# Revit family: Gravity_Intake_Roof_Ventilators-GLAB_Carnes
name_source: partatom
category: Mechanical Equipment
revit_build: Autodesk Revit Architecture 2012 (Build: 20110309_2315(x64)
units: mm (PartAtom-declared; Revit-internal decimal feet)

## types (117) — shared parameters
04 CSI = 23 34 23
95 CSI = 15830
Assembly Code = D3040200
Catalog URL = http://www.carnes.com
Default Elevation = 0' - 0"
Description = Gravity Intake Roof Ventilator
Housing = Aluminum-Carnes-Spun-Brushed
Manufacturer = Carnes Company
Manufacturer Fax = 608-845-6470
Material = Aluminum
Model = GLAB
Product Page URL = http://www.carnes.com
Specifications URL = http://www.carnes.com
Subcategory = Ventilation
URL = http://www.carnes.com
Warranty URL = http://www.carnes.com

## per-type parameters (varying)
| type | Curb Cap Length | Curb Cap Width | G | Hood Length | Hood Width | Intake Throat Velocity 1000 | Intake Throat Velocity 1200 | Intake Throat Velocity 400 | Intake Throat Velocity 500 | Intake Throat Velocity 600 | Intake Throat Velocity 700 | Intake Throat Velocity 800 | Intake Throat Velocity 900 | Louvers | Throat Area | Throat Size Length | Throat Size Width |
| 12x12 | 1' - 8" | 1' - 8" | 0' - 9 1/2" | 2' - 4" | 2' - 4" | 1000 | 1200 | 400 | 500 | 600 | 700 | 800 | 900 | 2 | 1.00 | 1' - 0" | 1' - 0" |
| 12x14 | 1' - 10" | 1' - 8" | 0' - 9 1/2" | 2' - 6" | 2' - 4" | 1167 | 1400 | 467 | 583 | 700 | 817 | 933 | 1050 | 2 | 1.17 | 1' - 2" | 1' - 0" |
| 12x16 | 2' - 0" | 1' - 8" | 0' - 9 1/2" | 2' - 8" | 2' - 4" | 1333 | 1600 | 533 | 667 | 800 | 933 | 1067 | 1200 | 2 | 1.33 | 1' - 4" | 1' - 0" |
| 12x18 | 2' - 2" | 1' - 8" | 0' - 9 1/2" | 2' - 10" | 2' - 4" | 1500 | 1800 | 600 | 750 | 900 | 1050 | 1200 | 1350 | 2 | 1.50 | 1' - 6" | 1' - 0" |
| 12x20 | 2' - 4" | 1' - 8" | 0' - 9 1/2" | 3' - 0" | 2' - 4" | 1667 | 2000 | 667 | 833 | 1000 | 1167 | 1333 | 1500 | 2 | 1.67 | 1' - 8" | 1' - 0" |
| 12x22 | 2' - 6" | 1' - 8" | 0' - 9 1/2" | 3' - 2" | 2' - 4" | 1833 | 2200 | 733 | 917 | 1100 | 1283 | 1467 | 1650 | 2 | 1.83 | 1' - 10" | 1' - 0" |
| 12x24 | 2' - 8" | 1' - 8" | 0' - 9 1/2" | 3' - 4" | 2' - 4" | 2000 | 2400 | 800 | 1000 | 1200 | 1400 | 1600 | 1800 | 2 | 2.00 | 2' - 0" | 1' - 0" |
| 12x30 | 3' - 2" | 1' - 8" | 0' - 9 1/2" | 3' - 10" | 2' - 4" | 2500 | 3000 | 1000 | 1250 | 1500 | 1750 | 2000 | 2250 | 2 | 2.50 | 2' - 6" | 1' - 0" |
| 12x36 | 3' - 8" | 1' - 8" | 0' - 9 1/2" | 4' - 4" | 2' - 4" | 3000 | 3600 | 1200 | 1500 | 1800 | 2100 | 2400 | 2700 | 2 | 3.00 | 3' - 0" | 1' - 0" |
| 12x42 | 4' - 2" | 1' - 8" | 0' - 9 1/2" | 4' - 10" | 2' - 4" | 3500 | 4200 | 1400 | 1750 | 2100 | 2450 | 2800 | 3150 | 2 | 3.50 | 3' - 6" | 1' - 0" |
| 12x48 | 4' - 8" | 1' - 8" | 0' - 9 1/2" | 5' - 4" | 2' - 4" | 4000 | 4800 | 1600 | 2000 | 2400 | 2800 | 3200 | 3600 | 2 | 4.00 | 4' - 0" | 1' - 0" |
| 12x54 | 5' - 2" | 1' - 8" | 0' - 9 1/2" | 5' - 10" | 2' - 4" | 4500 | 5400 | 1800 | 2250 | 2700 | 3150 | 3600 | 4050 | 2 | 4.50 | 4' - 6" | 1' - 0" |
| 14x14 | 1' - 10" | 1' - 10" | 0' - 9 1/2" | 2' - 6" | 2' - 6" | 1361 | 1633 | 544 | 681 | 817 | 953 | 1089 | 1225 | 2 | 1.36 | 1' - 2" | 1' - 2" |
| 14x16 | 2' - 0" | 1' - 10" | 0' - 9 1/2" | 2' - 8" | 2' - 6" | 1556 | 1867 | 622 | 778 | 933 | 1089 | 1244 | 1400 | 2 | 1.56 | 1' - 4" | 1' - 2" |
| 14x18 | 2' - 2" | 1' - 10" | 0' - 9 1/2" | 2' - 10" | 2' - 6" | 1750 | 2100 | 700 | 875 | 1050 | 1225 | 1400 | 1575 | 2 | 1.75 | 1' - 6" | 1' - 2" |
| 14x20 | 2' - 4" | 1' - 10" | 0' - 9 1/2" | 3' - 0" | 2' - 6" | 1944 | 2333 | 778 | 972 | 1167 | 1361 | 1556 | 1750 | 2 | 1.94 | 1' - 8" | 1' - 2" |
| 14x22 | 2' - 6" | 1' - 10" | 0' - 9 1/2" | 3' - 2" | 2' - 6" | 2139 | 2567 | 856 | 1069 | 1283 | 1497 | 1711 | 1925 | 2 | 2.14 | 1' - 10" | 1' - 2" |
| 14x24 | 2' - 8" | 1' - 10" | 0' - 9 1/2" | 3' - 4" | 2' - 6" | 2333 | 2800 | 933 | 1167 | 1400 | 1633 | 1867 | 2100 | 2 | 2.33 | 2' - 0" | 1' - 2" |
| 14x30 | 3' - 2" | 1' - 10" | 0' - 9 1/2" | 3' - 10" | 2' - 6" | 2917 | 3500 | 1167 | 1458 | 1750 | 2042 | 2333 | 2625 | 2 | 2.92 | 2' - 6" | 1' - 2" |
| 14x36 | 3' - 8" | 1' - 10" | 0' - 9 1/2" | 4' - 4" | 2' - 6" | 3500 | 4200 | 1400 | 1750 | 2100 | 2450 | 2800 | 3150 | 2 | 3.50 | 3' - 0" | 1' - 2" |
| 14x42 | 4' - 2" | 1' - 10" | 0' - 9 1/2" | 4' - 10" | 2' - 6" | 4083 | 4900 | 1633 | 2042 | 2450 | 2858 | 3267 | 3675 | 2 | 4.08 | 3' - 6" | 1' - 2" |
| 14x48 | 4' - 8" | 1' - 10" | 0' - 9 1/2" | 5' - 4" | 2' - 6" | 4667 | 5600 | 1867 | 2333 | 2800 | 3267 | 3733 | 4200 | 2 | 4.67 | 4' - 0" | 1' - 2" |
| 14x54 | 5' - 2" | 1' - 10" | 1' - 2" | 5' - 10" | 2' - 6" | 5250 | 6300 | 2100 | 2625 | 3150 | 3675 | 4200 | 4725 | 3 | 5.25 | 4' - 6" | 1' - 2" |
| 14x60 | 5' - 8" | 1' - 10" | 1' - 2" | 6' - 4" | 2' - 6" | 5833 | 7000 | 2333 | 2917 | 3500 | 4083 | 4667 | 5250 | 3 | 5.83 | 5' - 0" | 1' - 2" |
| 16x16 | 2' - 0" | 2' - 0" | 0' - 9 1/2" | 2' - 8" | 2' - 8" | 1778 | 2133 | 711 | 889 | 1067 | 1244 | 1422 | 1600 | 2 | 1.78 | 1' - 4" | 1' - 4" |
| 16x18 | 2' - 2" | 2' - 0" | 0' - 9 1/2" | 2' - 10" | 2' - 8" | 2000 | 2400 | 800 | 1000 | 1200 | 1400 | 1600 | 1800 | 2 | 2.00 | 1' - 6" | 1' - 4" |
| 16x20 | 2' - 4" | 2' - 0" | 0' - 9 1/2" | 3' - 0" | 2' - 8" | 2222 | 2667 | 889 | 1111 | 1333 | 1556 | 1778 | 2000 | 2 | 2.22 | 1' - 8" | 1' - 4" |
| 16x22 | 2' - 6" | 2' - 0" | 0' - 9 1/2" | 3' - 2" | 2' - 8" | 2444 | 2933 | 978 | 1222 | 1467 | 1711 | 1956 | 2200 | 2 | 2.44 | 1' - 10" | 1' - 4" |
| 16x24 | 2' - 8" | 2' - 0" | 0' - 9 1/2" | 3' - 4" | 2' - 8" | 2667 | 3200 | 1067 | 1333 | 1600 | 1867 | 2133 | 2400 | 2 | 2.67 | 2' - 0" | 1' - 4" |
| 16x30 | 3' - 2" | 2' - 0" | 0' - 9 1/2" | 3' - 10" | 2' - 8" | 3333 | 4000 | 1333 | 1667 | 2000 | 2333 | 2667 | 3000 | 2 | 3.33 | 2' - 6" | 1' - 4" |
| 16x36 | 3' - 8" | 2' - 0" | 1' - 2" | 4' - 4" | 2' - 8" | 4000 | 4800 | 1600 | 2000 | 2400 | 2800 | 3200 | 3600 | 3 | 4.00 | 3' - 0" | 1' - 4" |
| 16x42 | 4' - 2" | 2' - 0" | 1' - 2" | 4' - 10" | 2' - 8" | 4667 | 5600 | 1867 | 2333 | 2800 | 3267 | 3733 | 4200 | 3 | 4.67 | 3' - 6" | 1' - 4" |
| 16x48 | 4' - 8" | 2' - 0" | 1' - 2" | 5' - 4" | 2' - 8" | 5333 | 6400 | 2133 | 2667 | 3200 | 3733 | 4267 | 4800 | 3 | 5.33 | 4' - 0" | 1' - 4" |
| 16x54 | 5' - 2" | 2' - 0" | 1' - 2" | 5' - 10" | 2' - 8" | 6000 | 7200 | 2400 | 3000 | 3600 | 4200 | 4800 | 5400 | 3 | 6.00 | 4' - 6" | 1' - 4" |
| 16x60 | 5' - 8" | 2' - 0" | 1' - 2" | 6' - 4" | 2' - 8" | 6667 | 8000 | 2667 | 3333 | 4000 | 4667 | 5333 | 6000 | 3 | 6.67 | 5' - 0" | 1' - 4" |
| 16x72 | 6' - 8" | 2' - 0" | 1' - 2" | 7' - 4" | 2' - 8" | 8000 | 9600 | 3200 | 4000 | 4800 | 5600 | 6400 | 7200 | 3 | 8.00 | 6' - 0" | 1' - 4" |
| 18x18 | 2' - 2" | 2' - 2" | 0' - 9 1/2" | 2' - 10" | 2' - 10" | 2250 | 2700 | 900 | 1125 | 1350 | 1575 | 1800 | 2025 | 2 | 2.25 | 1' - 6" | 1' - 6" |
| 18x20 | 2' - 4" | 2' - 2" | 0' - 9 1/2" | 3' - 0" | 2' - 10" | 2500 | 3000 | 1000 | 1250 | 1500 | 1750 | 2000 | 2250 | 2 | 2.50 | 1' - 8" | 1' - 6" |
| 18x22 | 2' - 6" | 2' - 2" | 0' - 9 1/2" | 3' - 2" | 2' - 10" | 2750 | 3300 | 1100 | 1375 | 1650 | 1925 | 2200 | 2475 | 2 | 2.75 | 1' - 10" | 1' - 6" |
| 18x24 | 2' - 8" | 2' - 2" | 0' - 9" | 3' - 4" | 2' - 10" | 3000 | 3600 | 1200 | 1500 | 1800 | 2100 | 2400 | 2700 | 2 | 3.00 | 2' - 0" | 1' - 6" |
| 18x30 | 3' - 2" | 2' - 2" | 1' - 2" | 3' - 10" | 2' - 10" | 3750 | 4500 | 1500 | 1875 | 2250 | 2625 | 3000 | 3375 | 3 | 3.75 | 2' - 6" | 1' - 6" |
| 18x36 | 3' - 8" | 2' - 2" | 1' - 2" | 4' - 4" | 2' - 10" | 4500 | 5400 | 1800 | 2250 | 2700 | 3150 | 3600 | 4050 | 3 | 4.50 | 3' - 0" | 1' - 6" |
| 18x42 | 4' - 2" | 2' - 2" | 1' - 2" | 4' - 10" | 2' - 10" | 5250 | 6300 | 2100 | 2625 | 3150 | 3675 | 4200 | 4725 | 3 | 5.25 | 3' - 6" | 1' - 6" |
| 18x48 | 4' - 8" | 2' - 2" | 1' - 2" | 5' - 4" | 2' - 10" | 6000 | 7200 | 2400 | 3000 | 3600 | 4200 | 4800 | 5400 | 3 | 6.00 | 4' - 0" | 1' - 6" |
| 18x54 | 5' - 2" | 2' - 2" | 1' - 2" | 6' - 0" | 2' - 10" | 6750 | 8100 | 2700 | 3375 | 4050 | 4725 | 5400 | 6075 | 3 | 6.75 | 4' - 6" | 1' - 6" |
| 18x60 | 5' - 8" | 2' - 2" | 1' - 2" | 6' - 4" | 2' - 10" | 7500 | 9000 | 3000 | 3750 | 4500 | 5250 | 6000 | 6750 | 3 | 7.50 | 5' - 0" | 1' - 6" |
| 18x72 | 6' - 8" | 2' - 2" | 1' - 2" | 7' - 4" | 2' - 10" | 9000 | 10800 | 3600 | 4500 | 5400 | 6300 | 7200 | 8100 | 3 | 9.00 | 6' - 0" | 1' - 6" |
| 20x20 | 2' - 4" | 2' - 4" | 0' - 9 1/2" | 3' - 0" | 3' - 0" | 2778 | 3333 | 1111 | 1389 | 1667 | 1944 | 2222 | 2500 | 2 | 2.78 | 1' - 8" | 1' - 8" |
| 20x22 | 2' - 6" | 2' - 4" | 0' - 9 1/2" | 3' - 2" | 3' - 0" | 3056 | 3667 | 1222 | 1528 | 1833 | 2139 | 2444 | 2750 | 2 | 3.06 | 1' - 10" | 1' - 8" |
| 20x24 | 2' - 8" | 2' - 4" | 0' - 9 1/2" | 3' - 4" | 3' - 0" | 3333 | 4000 | 1333 | 1667 | 2000 | 2333 | 2667 | 3000 | 2 | 3.33 | 2' - 0" | 1' - 8" |
| 20x30 | 3' - 2" | 2' - 4" | 1' - 2" | 3' - 10" | 3' - 0" | 4167 | 5000 | 1667 | 2083 | 2500 | 2917 | 3333 | 3750 | 3 | 4.17 | 2' - 6" | 1' - 8" |
| 20x36 | 3' - 8" | 2' - 4" | 1' - 2" | 4' - 4" | 3' - 0" | 5000 | 6000 | 2000 | 2500 | 3000 | 3500 | 4000 | 4500 | 3 | 5.00 | 3' - 0" | 1' - 8" |
| 20x42 | 4' - 2" | 2' - 4" | 1' - 2" | 4' - 10" | 3' - 0" | 5833 | 7000 | 2333 | 2917 | 3500 | 4083 | 4667 | 5250 | 3 | 5.83 | 3' - 6" | 1' - 8" |
| 20x48 | 4' - 8" | 2' - 4" | 1' - 2" | 5' - 4" | 3' - 0" | 6667 | 8000 | 2667 | 3333 | 4000 | 4667 | 5333 | 6000 | 3 | 6.67 | 4' - 0" | 1' - 8" |
| 20x54 | 5' - 2" | 2' - 4" | 1' - 2" | 5' - 10" | 3' - 0" | 7500 | 9000 | 3000 | 3750 | 4500 | 5250 | 6000 | 6750 | 3 | 7.50 | 4' - 6" | 1' - 8" |
| 20x60 | 5' - 8" | 2' - 4" | 1' - 2" | 6' - 4" | 3' - 0" | 8333 | 10000 | 3333 | 4167 | 5000 | 5833 | 6667 | 7500 | 3 | 8.33 | 5' - 0" | 1' - 8" |
| 20x72 | 6' - 8" | 2' - 4" | 1' - 2" | 7' - 4" | 3' - 0" | 10000 | 12000 | 4000 | 5000 | 6000 | 7000 | 8000 | 9000 | 3 | 10.00 | 6' - 0" | 1' - 8" |
| 20x78 | 7' - 2" | 2' - 4" | 1' - 2" | 7' - 10" | 3' - 0" | 10833 | 13000 | 4333 | 5417 | 6500 | 7583 | 8667 | 9750 | 3 | 10.83 | 6' - 6" | 1' - 8" |
| 24x24 | 2' - 8" | 2' - 8" | 1' - 2" | 3' - 4" | 3' - 4" | 4000 | 4800 | 1600 | 2000 | 2400 | 2800 | 3200 | 3600 | 3 | 4.00 | 2' - 0" | 2' - 0" |
| 24x30 | 3' - 2" | 2' - 8" | 1' - 2" | 3' - 10" | 3' - 4" | 5000 | 6000 | 2000 | 2500 | 3000 | 3500 | 4000 | 4500 | 3 | 5.00 | 2' - 6" | 2' - 0" |
| 24x36 | 3' - 8" | 2' - 8" | 1' - 2" | 4' - 4" | 3' - 4" | 6000 | 7200 | 2400 | 3000 | 3600 | 4200 | 4800 | 5400 | 3 | 6.00 | 3' - 0" | 2' - 0" |
| 24x42 | 4' - 2" | 2' - 8" | 1' - 2" | 4' - 10" | 3' - 4" | 7000 | 8400 | 2800 | 3500 | 4200 | 4900 | 5600 | 6300 | 3 | 7.00 | 3' - 6" | 2' - 0" |
| 24x48 | 4' - 8" | 2' - 8" | 1' - 2" | 5' - 4" | 3' - 4" | 8000 | 9600 | 3200 | 4000 | 4800 | 5600 | 6400 | 7200 | 3 | 8.00 | 4' - 0" | 2' - 0" |
| 24x54 | 5' - 2" | 2' - 8" | 1' - 2" | 5' - 10" | 3' - 4" | 9000 | 10800 | 3600 | 4500 | 5400 | 6300 | 7200 | 8100 | 3 | 9.00 | 4' - 6" | 2' - 0" |
| 24x60 | 5' - 8" | 2' - 8" | 1' - 2" | 6' - 4" | 3' - 4" | 10000 | 12000 | 4000 | 5000 | 6000 | 7000 | 8000 | 9000 | 3 | 10.00 | 5' - 0" | 2' - 0" |
| 24x66 | 6' - 2" | 2' - 8" | 1' - 2" | 6' - 10" | 3' - 4" | 11000 | 13200 | 4400 | 5500 | 6600 | 7700 | 8800 | 9900 | 3 | 11.00 | 5' - 6" | 2' - 0" |
| 24x72 | 6' - 8" | 2' - 8" | 1' - 2" | 7' - 4" | 3' - 4" | 12000 | 14400 | 4800 | 6000 | 7200 | 8400 | 9600 | 10800 | 3 | 12.00 | 6' - 0" | 2' - 0" |
| 24x78 | 7' - 2" | 2' - 8" | 1' - 2" | 7' - 10" | 3' - 4" | 13000 | 15600 | 5200 | 6500 | 7800 | 9100 | 10400 | 11700 | 3 | 13.00 | 6' - 6" | 2' - 0" |
| 24x84 | 7' - 8" | 2' - 8" | 1' - 2" | 8' - 4" | 3' - 4" | 14000 | 16800 | 5600 | 7000 | 8400 | 9800 | 11200 | 12600 | 3 | 14.00 | 7' - 0" | 2' - 0" |
| 30x30 | 3' - 2" | 3' - 2" | 1' - 2" | 3' - 10" | 3' - 10" | 6250 | 7500 | 2500 | 3125 | 3750 | 4375 | 5000 | 5625 | 3 | 6.25 | 2' - 6" | 2' - 6" |
| 30x36 | 3' - 8" | 3' - 2" | 1' - 2" | 4' - 4" | 3' - 10" | 7500 | 9000 | 3000 | 3750 | 4500 | 5250 | 6000 | 6750 | 3 | 7.50 | 3' - 0" | 2' - 6" |
| 30x42 | 4' - 2" | 3' - 2" | 1' - 2" | 4' - 10" | 3' - 10" | 8750 | 10500 | 3500 | 4375 | 5250 | 6125 | 7000 | 7875 | 3 | 8.75 | 3' - 6" | 2' - 6" |
| 30x48 | 4' - 8" | 3' - 2" | 1' - 2" | 5' - 4" | 3' - 10" | 10000 | 12000 | 4000 | 5000 | 6000 | 7000 | 8000 | 9000 | 3 | 10.00 | 4' - 0" | 2' - 6" |
| 30x54 | 5' - 2" | 3' - 2" | 1' - 6 1/2" | 5' - 10" | 3' - 10" | 11250 | 13500 | 4500 | 5625 | 6750 | 7875 | 9000 | 10125 | 4 | 11.25 | 4' - 6" | 2' - 6" |
| 30x60 | 5' - 8" | 3' - 2" | 1' - 6 1/2" | 6' - 4" | 3' - 10" | 12500 | 15000 | 5000 | 6250 | 7500 | 8750 | 10000 | 11250 | 4 | 12.50 | 5' - 0" | 2' - 6" |
| 30x66 | 6' - 2" | 3' - 2" | 1' - 6 1/2" | 6' - 10" | 3' - 10" | 13750 | 16500 | 5500 | 6875 | 8250 | 9625 | 11000 | 12375 | 4 | 13.75 | 5' - 6" | 2' - 6" |
| 30x72 | 6' - 8" | 3' - 2" | 1' - 6 1/2" | 7' - 4" | 3' - 10" | 15000 | 18000 | 6000 | 7500 | 9000 | 10500 | 12000 | 13500 | 4 | 15.00 | 6' - 0" | 2' - 6" |
| 30x78 | 7' - 2" | 3' - 2" | 1' - 6 1/2" | 7' - 10" | 3' - 10" | 16250 | 19500 | 6500 | 8125 | 9750 | 11375 | 13000 | 14625 | 4 | 16.25 | 6' - 6" | 2' - 6" |
| 30x84 | 7' - 8" | 3' - 2" | 1' - 6 1/2" | 8' - 4" | 3' - 10" | 17500 | 21000 | 7000 | 8750 | 10500 | 12250 | 14000 | 15750 | 4 | 17.50 | 7' - 0" | 2' - 6" |
| 36x36 | 3' - 8" | 3' - 8" | 1' - 2" | 4' - 4" | 4' - 4" | 9000 | 10800 | 3600 | 4500 | 5400 | 6300 | 7200 | 8100 | 3 | 9.00 | 3' - 0" | 3' - 0" |
| 36x42 | 4' - 2" | 3' - 8" | 1' - 6 1/2" | 4' - 10" | 4' - 4" | 10500 | 12600 | 4200 | 5250 | 6300 | 7350 | 8400 | 9450 | 4 | 10.50 | 3' - 6" | 3' - 0" |
| 36x48 | 4' - 8" | 3' - 8" | 1' - 6 1/2" | 5' - 4" | 4' - 4" | 12000 | 14400 | 4800 | 6000 | 7200 | 8400 | 9600 | 10800 | 4 | 12.00 | 4' - 0" | 3' - 0" |
| 36x54 | 5' - 2" | 3' - 8" | 1' - 6 1/2" | 5' - 10" | 4' - 4" | 13500 | 16200 | 5400 | 6750 | 8100 | 9450 | 10800 | 12150 | 4 | 13.50 | 4' - 6" | 3' - 0" |
| 36x60 | 5' - 8" | 3' - 8" | 1' - 6 1/2" | 6' - 4" | 4' - 4" | 15000 | 18000 | 6000 | 7500 | 9000 | 10500 | 12000 | 13500 | 4 | 15.00 | 5' - 0" | 3' - 0" |
| 36x66 | 6' - 2" | 3' - 8" | 1' - 6 1/2" | 6' - 10" | 4' - 4" | 16500 | 19800 | 6600 | 8250 | 9900 | 11550 | 13200 | 14850 | 4 | 16.50 | 5' - 6" | 3' - 0" |
| 36x72 | 6' - 8" | 3' - 8" | 1' - 6 1/2" | 7' - 4" | 4' - 4" | 18000 | 21600 | 7200 | 9000 | 10800 | 12600 | 14400 | 16200 | 4 | 18.00 | 6' - 0" | 3' - 0" |
| 36x78 | 7' - 2" | 3' - 8" | 1' - 6 1/2" | 7' - 10" | 4' - 4" | 19500 | 23400 | 7800 | 9750 | 11700 | 13850 | 15600 | 17550 | 4 | 19.50 | 6' - 6" | 3' - 0" |
| 36x84 | 7' - 8" | 3' - 8" | 1' - 6 1/2" | 8' - 4" | 4' - 4" | 21000 | 25200 | 8400 | 10500 | 12600 | 14700 | 16800 | 18900 | 4 | 21.00 | 7' - 0" | 3' - 0" |
| 42x42 | 4' - 2" | 4' - 2" | 1' - 6 1/2" | 4' - 10" | 4' - 10" | 12250 | 14700 | 4900 | 6125 | 7350 | 8575 | 9800 | 11025 | 4 | 12.25 | 3' - 6" | 3' - 6" |
| 42x48 | 4' - 8" | 4' - 2" | 1' - 6 1/2" | 5' - 4" | 4' - 10" | 14000 | 16800 | 5600 | 7000 | 8400 | 9800 | 11200 | 12600 | 4 | 14.00 | 4' - 0" | 3' - 6" |
| 42x54 | 5' - 2" | 4' - 2" | 1' - 6 1/2" | 5' - 10" | 4' - 10" | 15750 | 18900 | 6300 | 7875 | 9450 | 11025 | 12600 | 14175 | 4 | 15.75 | 4' - 6" | 3' - 6" |
| 42x60 | 5' - 8" | 4' - 2" | 1' - 6 1/2" | 6' - 4" | 4' - 10" | 17500 | 21000 | 7000 | 8750 | 10500 | 12250 | 14000 | 15750 | 4 | 17.50 | 5' - 0" | 3' - 6" |
| 42x66 | 6' - 2" | 4' - 2" | 1' - 6 1/2" | 6' - 10" | 4' - 10" | 19250 | 23100 | 7700 | 9625 | 11550 | 13475 | 15400 | 17325 | 4 | 19.25 | 5' - 6" | 3' - 6" |
| 42x72 | 6' - 8" | 4' - 2" | 1' - 6 1/2" | 7' - 4" | 4' - 10" | 21000 | 25200 | 8400 | 10500 | 12600 | 14700 | 16800 | 18900 | 4 | 21.00 | 6' - 0" | 3' - 6" |
| 42x78 | 7' - 2" | 4' - 2" | 1' - 11" | 7' - 10" | 4' - 10" | 22750 | 27300 | 9100 | 11375 | 13650 | 15925 | 18200 | 20475 | 5 | 22.75 | 6' - 6" | 3' - 6" |
| 42x84 | 7' - 8" | 4' - 2" | 1' - 11" | 8' - 4" | 4' - 10" | 24500 | 29400 | 9800 | 12250 | 14700 | 17150 | 19600 | 22050 | 5 | 24.50 | 7' - 0" | 3' - 6" |
| 48x48 | 4' - 8" | 4' - 8" | 1' - 6 1/2" | 5' - 4" | 5' - 4" | 16000 | 19200 | 6400 | 8000 | 9600 | 11200 | 12800 | 14400 | 4 | 16.00 | 4' - 0" | 4' - 0" |
| 48x54 | 5' - 2" | 4' - 8" | 1' - 6 1/2" | 5' - 10" | 5' - 4" | 18000 | 21600 | 7200 | 9000 | 10800 | 12600 | 14400 | 16200 | 4 | 18.00 | 4' - 6" | 4' - 0" |
| 48x60 | 5' - 8" | 4' - 8" | 1' - 6 1/2" | 6' - 4" | 5' - 4" | 20000 | 24000 | 800 | 10000 | 12000 | 14000 | 16000 | 18000 | 4 | 20.00 | 5' - 0" | 4' - 0" |
| 48x66 | 6' - 2" | 4' - 8" | 1' - 11" | 6' - 10" | 5' - 4" | 22000 | 26400 | 8800 | 11000 | 13200 | 15400 | 17600 | 19800 | 5 | 22.00 | 5' - 6" | 4' - 0" |
| 48x72 | 6' - 8" | 4' - 8" | 1' - 11" | 7' - 4" | 5' - 4" | 24000 | 28800 | 9600 | 12000 | 14400 | 16800 | 19200 | 21600 | 5 | 24.00 | 6' - 0" | 4' - 0" |
| 48x78 | 7' - 2" | 4' - 8" | 1' - 11" | 7' - 10" | 5' - 4" | 26000 | 31200 | 10400 | 13000 | 15600 | 18200 | 20800 | 23400 | 5 | 26.00 | 6' - 6" | 4' - 0" |
| 48x84 | 7' - 8" | 4' - 8" | 1' - 11" | 8' - 4" | 5' - 4" | 28000 | 33600 | 11200 | 14000 | 16800 | 19600 | 22400 | 25200 | 5 | 28.00 | 7' - 0" | 4' - 0" |
| 54x54 | 5' - 2" | 5' - 2" | 1' - 11" | 5' - 10" | 5' - 10" | 20250 | 24300 | 8100 | 10125 | 12150 | 14175 | 16200 | 18225 | 5 | 20.25 | 4' - 6" | 4' - 6" |
| 54x60 | 5' - 8" | 5' - 2" | 1' - 11" | 6' - 4" | 5' - 10" | 22500 | 27000 | 9000 | 11250 | 13500 | 15750 | 18000 | 20250 | 5 | 22.50 | 5' - 0" | 4' - 6" |
| 54x66 | 6' - 2" | 5' - 2" | 1' - 11" | 6' - 10" | 5' - 10" | 24750 | 29700 | 9900 | 12375 | 14850 | 17325 | 19800 | 22275 | 5 | 24.75 | 5' - 6" | 4' - 6" |
| 54x72 | 6' - 8" | 5' - 2" | 1' - 11" | 7' - 4" | 5' - 10" | 27000 | 32400 | 10800 | 13500 | 16200 | 18900 | 21600 | 24300 | 5 | 27.00 | 6' - 0" | 4' - 6" |
| 54x78 | 7' - 2" | 5' - 2" | 1' - 11" | 7' - 10" | 5' - 10" | 29250 | 35100 | 11700 | 14625 | 17550 | 20475 | 23400 | 26325 | 5 | 29.25 | 6' - 6" | 4' - 6" |
| 54x84 | 7' - 8" | 5' - 2" | 1' - 11" | 8' - 4" | 5' - 10" | 31500 | 37800 | 12600 | 15750 | 18900 | 22050 | 25200 | 28350 | 5 | 31.50 | 7' - 0" | 4' - 6" |
| 60x60 | 5' - 8" | 5' - 8" | 1' - 11" | 6' - 4" | 6' - 4" | 25000 | 30000 | 10000 | 12500 | 15000 | 17500 | 20000 | 22500 | 5 | 25.00 | 5' - 0" | 5' - 0" |
| 60x66 | 6' - 2" | 5' - 8" | 1' - 11" | 6' - 10" | 6' - 4" | 27500 | 33000 | 11000 | 13750 | 16500 | 19250 | 22000 | 24750 | 5 | 27.50 | 5' - 6" | 5' - 0" |
| 60x72 | 6' - 8" | 5' - 8" | 1' - 11" | 7' - 4" | 6' - 4" | 30000 | 36000 | 12000 | 15000 | 18000 | 21000 | 24000 | 27000 | 5 | 30.00 | 6' - 0" | 5' - 0" |
| 60x84 | 7' - 8" | 5' - 8" | 2' - 3 1/2" | 8' - 4" | 6' - 4" | 35000 | 42000 | 14000 | 17500 | 21000 | 24500 | 28000 | 31500 | 6 | 35.00 | 7' - 0" | 5' - 0" |
| 66x66 | 6' - 2" | 6' - 2" | 1' - 11" | 6' - 10" | 6' - 10" | 30250 | 36300 | 12100 | 15125 | 18150 | 21175 | 24200 | 27225 | 5 | 30.25 | 5' - 6" | 5' - 6" |
| 66x72 | 6' - 8" | 6' - 2" | 1' - 11" | 7' - 4" | 6' - 10" | 33000 | 39600 | 13200 | 16500 | 19800 | 23100 | 26400 | 29700 | 5 | 33.00 | 6' - 0" | 5' - 6" |
| 66x78 | 7' - 2" | 6' - 2" | 2' - 3 1/2" | 7' - 10" | 6' - 10" | 35750 | 42900 | 14300 | 17875 | 21450 | 25025 | 28600 | 32175 | 6 | 35.75 | 6' - 6" | 5' - 6" |
| 66x84 | 7' - 8" | 6' - 2" | 2' - 3 1/2" | 8' - 4" | 6' - 10" | 38500 | 46200 | 15400 | 19250 | 23100 | 26950 | 30800 | 34650 | 6 | 38.50 | 7' - 0" | 5' - 6" |

## geometry (parser evidence)
native form markers: Sweep x6
no freeform markers — native parametric forms only
